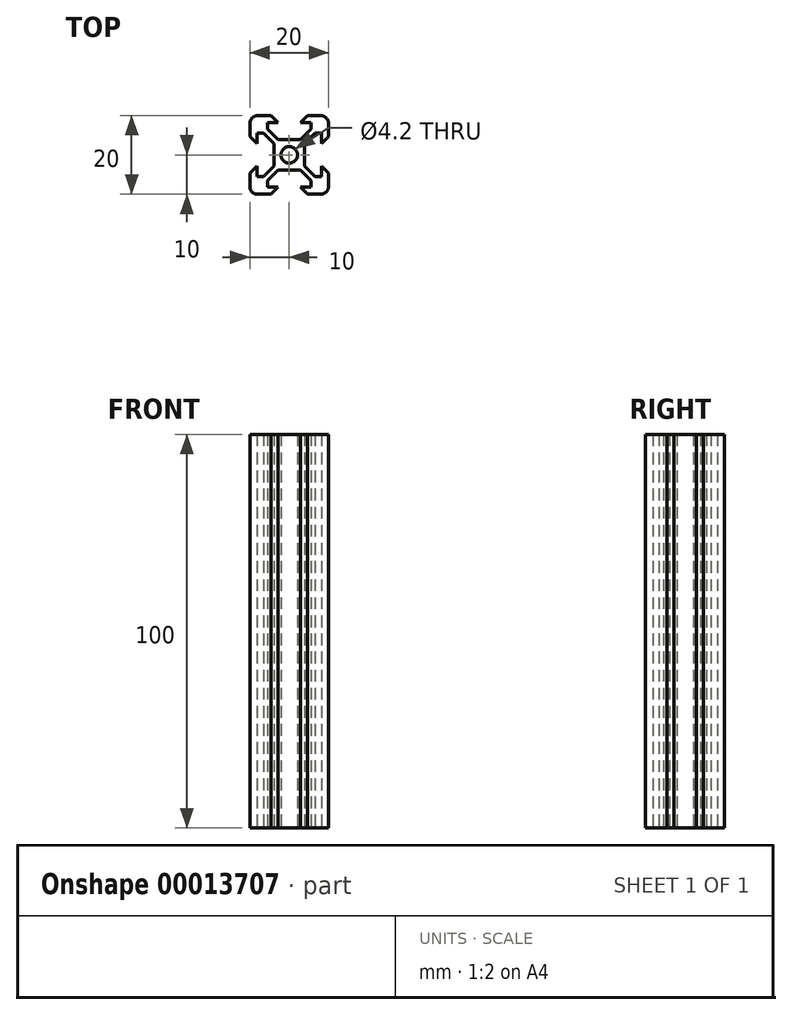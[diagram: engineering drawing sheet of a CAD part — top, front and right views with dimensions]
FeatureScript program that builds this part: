
annotation { "Feature Type Name" : "Feature", "Feature Type Description" : "" }
export const myFeature = defineFeature(function(context is Context, id is Id, definition is map)
    precondition{}
    {
        {
            var Q0;
            Q0=qCreatedBy(makeId("Top.planeOp"),FACE);
            var sketch = newSketch(context, id + "F0", { "sketchPlane" : qUnion([Q0])});
            skCircle(sketch, "E0", {"center": v(0, 0) * mm, "radius": 2.1 * mm});
            skLineSegment(sketch, "E1.rect.bottom", {"start": v(8, 10) * mm, "end": v(4.64, 10) * mm});
            skLineSegment(sketch, "E1.rect.top", {"start": v(8, -10) * mm, "end": v(4.64, -10) * mm});
            skLineSegment(sketch, "E1.rect.left", {"start": v(10, 8) * mm, "end": v(10, 4.64) * mm});
            skLineSegment(sketch, "E1.rect.right", {"start": v(-10, 8) * mm, "end": v(-10, 4.64) * mm});
            skLineSegment(sketch, "E2.0", {"start": v(5.5, 8.2) * mm, "end": v(2.84, 8.2) * mm});
            skLineSegment(sketch, "E2.1", {"start": v(8.2, 5.5) * mm, "end": v(8.2, 2.84) * mm});
            skLineSegment(sketch, "E2.2", {"start": v(5.5, -8.2) * mm, "end": v(2.84, -8.2) * mm});
            skLineSegment(sketch, "E2.3", {"start": v(-8.2, 5.5) * mm, "end": v(-8.2, 2.84) * mm});
            skLineSegment(sketch, "E3.0", {"start": v(6.56, 6.56) * mm, "end": v(-6.56, 6.56) * mm, "construction": true});
            skLineSegment(sketch, "E3.1", {"start": v(6.56, 6.56) * mm, "end": v(6.56, -6.56) * mm, "construction": true});
            skLineSegment(sketch, "E3.2", {"start": v(6.56, -6.56) * mm, "end": v(-6.56, -6.56) * mm, "construction": true});
            skLineSegment(sketch, "E3.3", {"start": v(-6.56, 6.56) * mm, "end": v(-6.56, -6.56) * mm, "construction": true});
            skLineSegment(sketch, "E4", {"start": v(0, 0) * mm, "end": v(-10, 10) * mm, "construction": true});
            skLineSegment(sketch, "E5", {"start": v(0, 0) * mm, "end": v(10, 10) * mm, "construction": true});
            skLineSegment(sketch, "E6", {"start": v(0, 0) * mm, "end": v(10, -10) * mm, "construction": true});
            skLineSegment(sketch, "E7", {"start": v(0, 0) * mm, "end": v(-10, -10) * mm, "construction": true});
            skLineSegment(sketch, "E8", {"start": v(-3.9, 2.84) * mm, "end": v(-3.9, -2.84) * mm});
            skLineSegment(sketch, "E9", {"start": v(-2.84, -3.9) * mm, "end": v(2.84, -3.9) * mm});
            skLineSegment(sketch, "E10", {"start": v(3.9, -2.84) * mm, "end": v(3.9, 2.84) * mm});
            skLineSegment(sketch, "E11", {"start": v(-2.84, 3.9) * mm, "end": v(2.84, 3.9) * mm});
            skLineSegment(sketch, "E12", {"start": v(0, 3.9) * mm, "end": v(0, 0) * mm, "construction": true});
            skLineSegment(sketch, "E13", {"start": v(3.9, 0) * mm, "end": v(0, 0) * mm, "construction": true});
            skLineSegment(sketch, "E14", {"start": v(0, -3.9) * mm, "end": v(0, 0) * mm, "construction": true});
            skLineSegment(sketch, "E15", {"start": v(-3.9, 0) * mm, "end": v(0, 0) * mm, "construction": true});
            skLineSegment(sketch, "E16", {"start": v(-2.84, 3.9) * mm, "end": v(-5.5, 6.56) * mm});
            skLineSegment(sketch, "E17", {"start": v(-3.9, 2.84) * mm, "end": v(-6.56, 5.5) * mm});
            skLineSegment(sketch, "E18", {"start": v(2.84, 3.9) * mm, "end": v(5.5, 6.56) * mm});
            skLineSegment(sketch, "E19", {"start": v(3.9, 2.84) * mm, "end": v(6.56, 5.5) * mm});
            skLineSegment(sketch, "E20", {"start": v(3.9, -2.84) * mm, "end": v(6.56, -5.5) * mm});
            skLineSegment(sketch, "E21", {"start": v(2.84, -3.9) * mm, "end": v(5.5, -6.56) * mm});
            skLineSegment(sketch, "E22", {"start": v(-2.84, -3.9) * mm, "end": v(-5.5, -6.56) * mm});
            skLineSegment(sketch, "E23", {"start": v(-3.9, -2.84) * mm, "end": v(-6.56, -5.5) * mm});
            skLineSegment(sketch, "E24", {"start": v(-5.5, -6.56) * mm, "end": v(-5.5, -8.2) * mm});
            skLineSegment(sketch, "E25", {"start": v(-6.56, -5.5) * mm, "end": v(-8.2, -5.5) * mm});
            skLineSegment(sketch, "E26", {"start": v(6.56, -5.5) * mm, "end": v(8.2, -5.5) * mm});
            skLineSegment(sketch, "E27", {"start": v(5.5, -6.56) * mm, "end": v(5.5, -8.2) * mm});
            skLineSegment(sketch, "E28", {"start": v(6.56, 5.5) * mm, "end": v(8.2, 5.5) * mm});
            skLineSegment(sketch, "E29", {"start": v(5.5, 6.56) * mm, "end": v(5.5, 8.2) * mm});
            skLineSegment(sketch, "E30", {"start": v(-5.5, 6.56) * mm, "end": v(-5.5, 8.2) * mm});
            skLineSegment(sketch, "E31", {"start": v(-6.56, 5.5) * mm, "end": v(-8.2, 5.5) * mm});
            skLineSegment(sketch, "E32", {"start": v(-8.2, -2.84) * mm, "end": v(-10, -4.64) * mm});
            skLineSegment(sketch, "E33", {"start": v(-8.2, 2.84) * mm, "end": v(-10, 4.64) * mm});
            skLineSegment(sketch, "E34", {"start": v(-2.84, 8.2) * mm, "end": v(-4.64, 10) * mm});
            skLineSegment(sketch, "E35", {"start": v(2.84, 8.2) * mm, "end": v(4.64, 10) * mm});
            skLineSegment(sketch, "E36", {"start": v(8.2, 2.84) * mm, "end": v(10, 4.64) * mm});
            skLineSegment(sketch, "E37", {"start": v(8.2, -2.84) * mm, "end": v(10, -4.64) * mm});
            skLineSegment(sketch, "E38", {"start": v(2.84, -8.2) * mm, "end": v(4.64, -10) * mm});
            skLineSegment(sketch, "E39", {"start": v(-2.84, -8.2) * mm, "end": v(-4.64, -10) * mm});
            skLineSegment(sketch, "E40.trimOffspring", {"start": v(-2.84, -8.2) * mm, "end": v(-5.5, -8.2) * mm});
            skLineSegment(sketch, "E41.trimOffspring", {"start": v(8.2, -2.84) * mm, "end": v(8.2, -5.5) * mm});
            skLineSegment(sketch, "E42.trimOffspring", {"start": v(-2.84, 8.2) * mm, "end": v(-5.5, 8.2) * mm});
            skLineSegment(sketch, "E43.trimOffspring", {"start": v(-8.2, -2.84) * mm, "end": v(-8.2, -5.5) * mm});
            skLineSegment(sketch, "E44.trimOffspring", {"start": v(-10, -4.64) * mm, "end": v(-10, -8) * mm});
            skLineSegment(sketch, "E45.trimOffspring", {"start": v(-4.64, 10) * mm, "end": v(-8, 10) * mm});
            skLineSegment(sketch, "E46.trimOffspring", {"start": v(10, -4.64) * mm, "end": v(10, -8) * mm});
            skLineSegment(sketch, "E47.trimOffspring", {"start": v(-4.64, -10) * mm, "end": v(-8, -10) * mm});
            skPoint(sketch, "E48.visualSharp", {"position": v(10, 10) * mm});
            skArc(sketch, "E48.filletArc", {"start": v(10, 8) * mm, "mid": v(9.41, 9.41) * mm, "end": v(8, 10) * mm});
            skPoint(sketch, "E49.visualSharp", {"position": v(10, -10) * mm});
            skArc(sketch, "E49.filletArc", {"start": v(8, -10) * mm, "mid": v(9.41, -9.41) * mm, "end": v(10, -8) * mm});
            skPoint(sketch, "E50.visualSharp", {"position": v(-10, -10) * mm});
            skArc(sketch, "E50.filletArc", {"start": v(-10, -8) * mm, "mid": v(-9.41, -9.41) * mm, "end": v(-8, -10) * mm});
            skPoint(sketch, "E51.visualSharp", {"position": v(-10, 10) * mm});
            skArc(sketch, "E51.filletArc", {"start": v(-8, 10) * mm, "mid": v(-9.41, 9.41) * mm, "end": v(-10, 8) * mm});
            skSolve(sketch);
        }
        {
            var Q0;
            Q0=makeQuery(id+"F0.imprint","IMPRINT",FACE,{"disambiguationData":[TD([[makeQuery(id+"F0.imprint","IMPRINT",EDGE,{"derivedFrom":sQuery(id+"F0.wireOp",EDGE,"E0")}),-1.0]])]});
            extrude(context, id + "F1", {"entities" : qUnion([Q0]), "depth" : 100 * mm});
        }
    });
